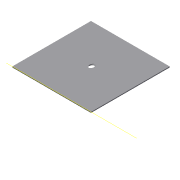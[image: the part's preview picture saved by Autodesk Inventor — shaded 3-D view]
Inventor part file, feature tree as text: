
AUTODESK INVENTOR PART (.ipt)
format: ipt  version: 2019.4 (Build 234330000, 330)  size: 94,720 bytes
history: native  units: mm
features: extrude x3, sketch x3, plane x2, projected_geometry x2
ambient origin geometry x8: Origin, YZ Plane, XZ Plane, XY Plane, X Axis, Y Axis, Z Axis, Center Point
bodies: Solid1 (feature_tree)
feature tree (10):
  extrude  "Extrusion1"  Depth=18.0mm
  plane  "Work Plane1"
  extrude  "Extrusion2"  Depth=0.2mm
  plane  "Work Plane2"
  extrude  "Extrusion3"  Depth=0.2mm
  sketch  "Sketch1"  dims[d0=18.0mm d1=18.0mm]
  sketch  "Sketch2"  dims[d2=0.2mm d3=0.0mm d4=1.0mm]
  projected_geometry  "Projected Loop1"
  sketch  "Sketch3"  dims[d5=0.2mm d6=0.0mm d7=1.0mm d8=0.2mm d9=0.0mm]
  projected_geometry  "Projected Loop2"
